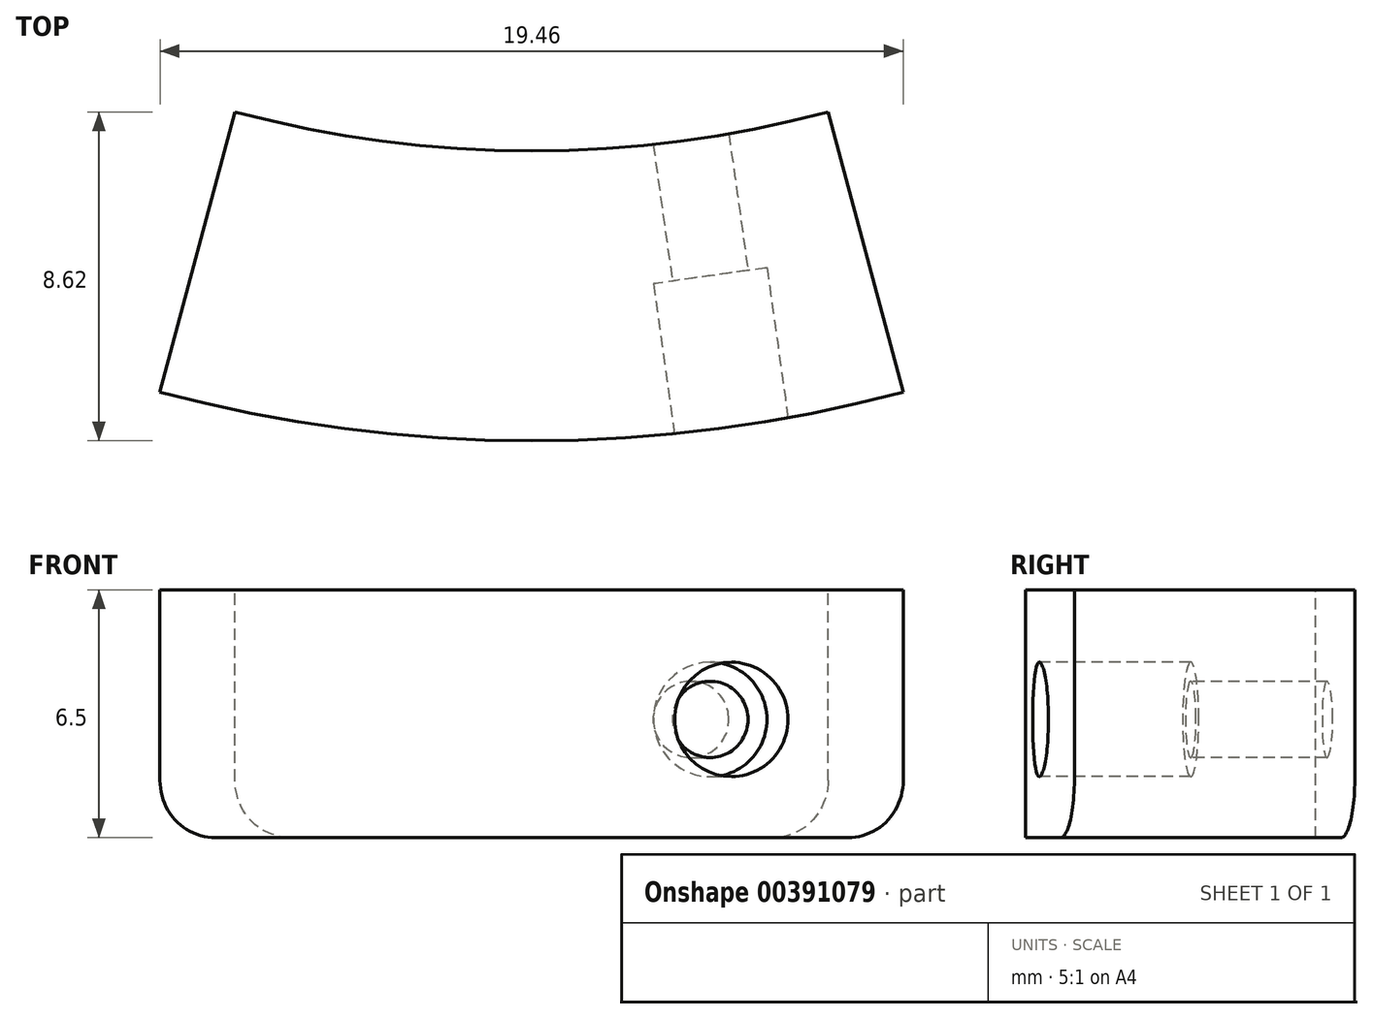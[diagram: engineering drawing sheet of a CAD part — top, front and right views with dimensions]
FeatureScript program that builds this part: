
annotation { "Feature Type Name" : "Feature", "Feature Type Description" : "" }
export const myFeature = defineFeature(function(context is Context, id is Id, definition is map)
    precondition{}
    {
        {
            var Q0;
            Q0=qCreatedBy(makeId("Top.planeOp"),FACE);
            var sketch = newSketch(context, id + "F0", { "sketchPlane" : qUnion([Q0])});
            skCircle(sketch, "E0", {"center": v(0, 0) * mm, "radius": 32 * mm});
            skCircle(sketch, "E1", {"center": v(0, 0) * mm, "radius": 37.6 * mm});
            skLineSegment(sketch, "E2", {"start": v(0, 0) * mm, "end": v(37.36, -4.23) * mm, "construction": true});
            skLineSegment(sketch, "E3", {"start": v(-4.66, -33.17) * mm, "end": v(-4.77, -33.97) * mm, "construction": true});
            skArc(sketch, "E4", {"start": v(-5.56, -33.85) * mm, "mid": v(-5.17, -33.9) * mm, "end": v(-4.77, -33.97) * mm, "construction": true});
            skLineSegment(sketch, "E5", {"start": v(-8.28, -30.9) * mm, "end": v(-9.73, -36.32) * mm});
            skLineSegment(sketch, "E6", {"start": v(0, 0) * mm, "end": v(9.73, -36.32) * mm});
            skPoint(sketch, "E7", {"position": v(34.58, -3.92) * mm});
            skArc(sketch, "E8", {"start": v(37.36, -4.23) * mm, "mid": v(34.9, -1.13) * mm, "end": v(31.8, -3.6) * mm});
            skLineSegment(sketch, "E9", {"start": v(30.07, -10.94) * mm, "end": v(35.33, -12.86) * mm, "construction": true});
            skCircle(sketch, "E10", {"center": v(34.58, -3.92) * mm, "radius": 1.65 * mm});
            skCircle(sketch, "E11", {"center": v(0, 0) * mm, "radius": 30 * mm});
            skLineSegment(sketch, "E12", {"start": v(-8.28, -30.9) * mm, "end": v(-7.76, -28.98) * mm});
            skLineSegment(sketch, "E13", {"start": v(0, 0) * mm, "end": v(4.18, -29.7) * mm, "construction": true});
            skLineSegment(sketch, "E14", {"start": v(0, 0) * mm, "end": v(-4.18, -29.7) * mm, "construction": true});
            skSolve(sketch);
        }
        {
            var Q0;
            Q0=makeQuery(id+"F0.imprint","IMPRINT",FACE,{"disambiguationData":[TD([[makeQuery(id+"F0.imprint","IMPRINT",EDGE,{"derivedFrom":sQuery(id+"F0.wireOp",EDGE,"z00oiAul-z2WD-jYly-T4Gg-m5JlJ8elssB2")}),-1.0]])]});
            var Q1;
            Q1=makeQuery(id+"F0.imprint","IMPRINT",FACE,{"disambiguationData":[TD([[makeQuery(id+"F0.imprint","IMPRINT",EDGE,{"derivedFrom":sQuery(id+"F0.wireOp",EDGE,"cpbOuPma-2R4H-8ffu-GBJo-bnfGFGacq3pO")}),-1.0]])]});
            var Q2;
            {var subQ0=sQuery(id+"F0.wireOp",EDGE,"E5");Q2=makeQuery(id+"F0.imprint","IMPRINT",FACE,{"disambiguationData":[TD([[makeQuery(id+"F0.imprint","IMPRINT",EDGE,{"derivedFrom":subQ0}),1.0]])]});}
            extrude(context, id + "F1", {"entities" : qUnion([Q0, Q1, Q2]), "oppositeDirection" : true, "depth" : 3 * mm});
        }
        {
            var Q0;
            {var subQ0=sQuery(id+"F0.wireOp",EDGE,"E12");Q0=makeQuery(id+"F0.imprint","IMPRINT",FACE,{"disambiguationData":[TD([[makeQuery(id+"F0.imprint","IMPRINT",EDGE,{"derivedFrom":subQ0}),-1.0]])]});}
            var Q1;
            {var subQ0=sQuery(id+"F0.wireOp",EDGE,"E5");Q1=makeQuery(id+"F0.imprint","IMPRINT",FACE,{"disambiguationData":[TD([[makeQuery(id+"F0.imprint","IMPRINT",EDGE,{"derivedFrom":subQ0}),1.0]])]});}
            extrude(context, id + "F2", {"entities" : qUnion([Q0, Q1]), "operationType" : NewBodyOperationType.ADD, "oppositeDirection" : true, "depth" : 6.5 * mm});
        }
        {
            var Q0;
            {var subQ0=sQuery(id+"F0.wireOp",EDGE,"E5");Q0=makeQuery(id+"F0.imprint","IMPRINT",FACE,{"disambiguationData":[TD([[makeQuery(id+"F0.imprint","IMPRINT",EDGE,{"derivedFrom":subQ0}),1.0]])]});}
            cPlane(context, id + "F3", {"entities" : qUnion([Q0]), "cplaneType" : CPlaneType.OFFSET, "offset" : 3.4 * mm, "oppositeDirection" : true, "width" : 150 * mm, "height" : 150 * mm});
        }
        {
            var Q0;
            Q0=qCreatedBy(id+"F3.planeOp",FACE);
            var sketch = newSketch(context, id + "F4", { "sketchPlane" : qUnion([Q0])});
            skPoint(sketch, "E15.0", {"position": v(4.18, -29.7) * mm});
            skLineSegment(sketch, "E15.1", {"start": v(0, 0) * mm, "end": v(4.18, -29.7) * mm, "construction": true});
            skArc(sketch, "E16.1", {"start": v(-7.76, -28.98) * mm, "mid": v(0, -30) * mm, "end": v(7.76, -28.98) * mm});
            skLineSegment(sketch, "E17.0", {"start": v(-9.73, -36.32) * mm, "end": v(-9.73, -36.32) * mm});
            skLineSegment(sketch, "E18", {"start": v(4.18, -29.7) * mm, "end": v(5.23, -37.23) * mm, "construction": true});
            skSolve(sketch);
        }
        {
            var Q0;
            Q0=sQuery(id+"F4.wireOp",VERTEX,"E15.0");
            var Q1;
            Q1=sQuery(id+"F4.wireOp",EDGE,"E15.1");
            cPlane(context, id + "F5", {"entities" : qUnion([Q0, Q1]), "cplaneType" : CPlaneType.LINE_POINT, "offset" : 25 * mm, "width" : 150 * mm, "height" : 150 * mm});
        }
        {
            var Q0;
            Q0=qCreatedBy(id+"F5.planeOp",FACE);
            var sketch = newSketch(context, id + "F6", { "sketchPlane" : qUnion([Q0])});
            skPoint(sketch, "E19.0", {"position": v(0, -3.4) * mm});
            skCircle(sketch, "E20", {"center": v(0, -3.4) * mm, "radius": 1 * mm});
            skSolve(sketch);
        }
        {
            var Q0;
            Q0=qSketchRegion(id+"F6",true);
            extrude(context, id + "F7", {"entities" : qUnion([Q0]), "operationType" : NewBodyOperationType.REMOVE, "endBound" : BoundingType.SYMMETRIC, "oppositeDirection" : true, "depth" : 25 * mm});
        }
        {
            var Q0;
            Q0=makeQuery(id+"F2.opExtrude","CAP_EDGE",EDGE,{"disambiguationData":[OSD([sQuery(id+"F0.wireOp",EDGE,"E5"),sQuery(id+"F0.wireOp",EDGE,"E12")])],"isStart":false});
            var Q1;
            Q1=makeQuery(id+"F2.opExtrude","CAP_EDGE",EDGE,{"disambiguationData":[OSD([sQuery(id+"F0.wireOp",EDGE,"E6")])],"isStart":false});
            var Q2;
            Q2=makeQuery(id+"F2.boolean.opBoolean","INTERSECT",EDGE,{"derivedFrom":[makeQuery(id+"F1.opExtrude","CAP_FACE",FACE,{"disambiguationData":[OSD([sQuery(id+"F0.wireOp",EDGE,"E0"),sQuery(id+"F0.wireOp",EDGE,"E1"),sQuery(id+"F0.wireOp",EDGE,"E5"),sQuery(id+"F0.wireOp",EDGE,"E8"),sQuery(id+"F0.wireOp",EDGE,"cpbOuPma-2R4H-8ffu-GBJo-bnfGFGacq3pO")])],"isStart":false}),makeQuery(id+"F2.opExtrude","SWEPT_FACE",FACE,{"disambiguationData":[OSD([sQuery(id+"F0.wireOp",EDGE,"E6")])]})]});
            var Q3;
            Q3=makeQuery(id+"F2.boolean.opBoolean","INTERSECT",EDGE,{"derivedFrom":[makeQuery(id+"F1.opExtrude","SWEPT_FACE",FACE,{"disambiguationData":[OSD([sQuery(id+"F0.wireOp",EDGE,"E0")])]}),makeQuery(id+"F2.opExtrude","SWEPT_FACE",FACE,{"disambiguationData":[OSD([sQuery(id+"F0.wireOp",EDGE,"E6")])]})]});
            fillet(context, id + "F8", {"entities" : qUnion([Q0, Q1, Q2, Q3]), "radius" : 1.5 * mm, "tangentPropagation" : true, "allowEdgeOverflow" : false});
        }
        {
            var Q0;
            Q0=sQuery(id+"F4.wireOp",VERTEX,"E18.end");
            var Q1;
            Q1=sQuery(id+"F4.wireOp",EDGE,"E18");
            cPlane(context, id + "F9", {"entities" : qUnion([Q0, Q1]), "cplaneType" : CPlaneType.LINE_POINT, "offset" : 25 * mm, "width" : 150 * mm, "height" : 150 * mm});
        }
        {
            var Q0;
            Q0=qCreatedBy(id+"F9.planeOp",FACE);
            var sketch = newSketch(context, id + "F10", { "sketchPlane" : qUnion([Q0])});
            skPoint(sketch, "E21.0", {"position": v(0, -3.4) * mm});
            skCircle(sketch, "E22", {"center": v(0, -3.4) * mm, "radius": 1.5 * mm});
            skSolve(sketch);
        }
        {
            var Q0;
            Q0=makeQuery(id+"F10.imprint","IMPRINT",FACE,{"disambiguationData":[TD([[makeQuery(id+"F10.imprint","IMPRINT",EDGE,{"derivedFrom":sQuery(id+"F10.wireOp",EDGE,"E22")}),1.0]])]});
            extrude(context, id + "F11", {"entities" : qUnion([Q0]), "operationType" : NewBodyOperationType.REMOVE, "oppositeDirection" : true, "depth" : 4 * mm, "offsetDistance" : 25 * mm});
        }
    });
